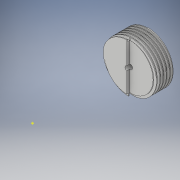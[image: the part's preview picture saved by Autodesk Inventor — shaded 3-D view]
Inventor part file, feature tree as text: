
AUTODESK INVENTOR PART (.ipt)
format: ipt  version: 2018 (Build 220112000, 112)  size: 623,104 bytes
history: native  units: in
note: dims shown in document units (in); Inventor stores cm internally (conversion verified against a paired STEP export)
features: sketch x6, helix x3, extrude x3, other x2, plane x1, loft x1, hole x1, projected_geometry x1
ambient origin geometry x8: Origin, YZ Plane, XZ Plane, XY Plane, X Axis, Y Axis, Z Axis, Center Point
bodies: Solid1 (feature_tree)
feature tree (18):
  sketch  "Sketch1"  dims[d0=2.0in d2=3.9in]
  plane  "Work Plane1"
  loft  "Loft1"
  other  "Work Point1"
  hole  "Hole1"  [1 undecoded]
  other  "Work Axis2"
  sketch  "Sketch6"  dims[d83=1.0in d84=1.0in d11=0.18in d12=0.75in d13=0.375in d14=0.25in d15=0.5635in d16=1.0in d17=0.8108in d41=0.1in]
  helix  "Coil3"  [1 undecoded]
  helix  "Coil4"  [1 undecoded]
  sketch  "Sketch8"  dims[d42=0.1in d43=0.02in]
  extrude  "Extrusion2"  Depth=0.02in
  helix  "Coil5"  [1 undecoded]
  extrude  "Extrusion3"  Depth=0.125in TaperAngle=0.0deg
  extrude  "Extrusion4"  Depth=0.125in
  sketch  "Sketch2"  dims[d3=0.5in d5=0.0in d6=90.0deg d7=0.0in d8=90.0deg]
  projected_geometry  "Projected Loop1"
  sketch  "Sketch9"  dims[d44=0.13in d45=1.0in d46=11.811in d47=-0.0739in d48=90.0deg d49=90.0deg d50=0.0in d51=0.0in]
  sketch  "Sketch11"  dims[d52=0.13in d53=1.0in d54=11.811in d55=0.0756in d56=90.0deg d57=90.0deg d58=0.0in d59=0.0in d61=0.7in d62=0.0in d65=0.13in d66=1.0in d67=2.3622in d68=0.0in d69=90.0deg d70=90.0deg d71=0.0in d72=0.0in d75=3.0in d76=0.0in d78=1.2in d79=1.18in d80=1.2in d81=1.0in d82=0.125in d85=0.18in d86=3.0in d87=0.0in]
note: 4 required parameter values undecoded (feature->parameter linkage not recoverable at this tier; creation-order binding heuristic only, values carry confidence <= 0.55)
